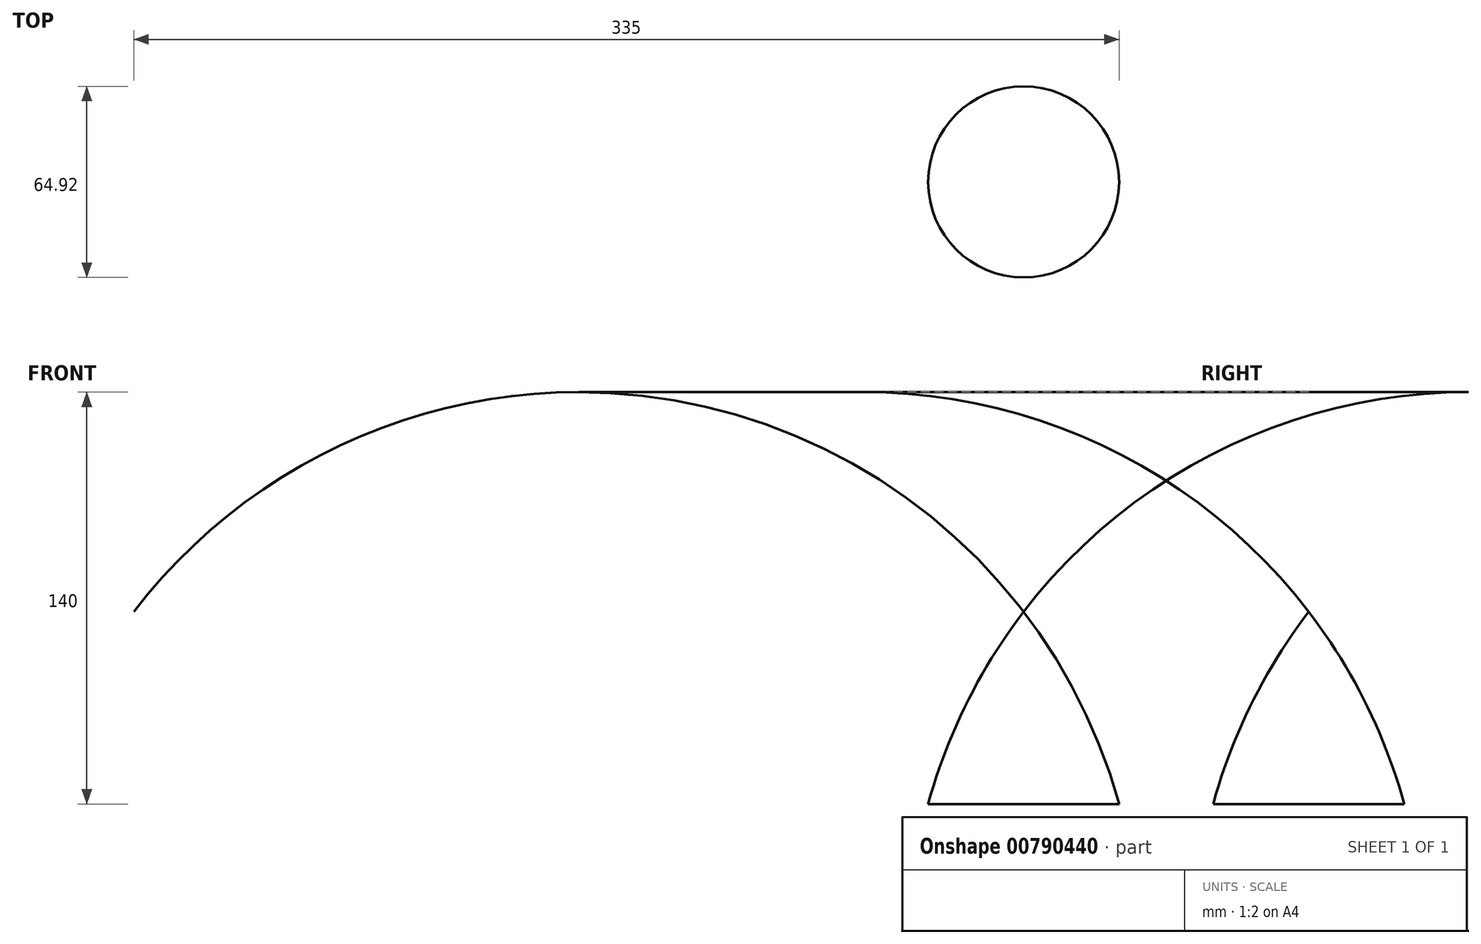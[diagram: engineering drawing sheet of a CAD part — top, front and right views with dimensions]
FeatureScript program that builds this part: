
annotation { "Feature Type Name" : "Feature", "Feature Type Description" : "" }
export const myFeature = defineFeature(function(context is Context, id is Id, definition is map)
    precondition{}
    {
        {
            var Q0;
            Q0=qCreatedBy(makeId("Front.planeOp"),FACE);
            var sketch = newSketch(context, id + "F0", { "sketchPlane" : qUnion([Q0])});
            skLineSegment(sketch, "E0", {"start": v(0, 0) * mm, "end": v(32.46, 0) * mm});
            skLineSegment(sketch, "E1", {"start": v(32.46, 0) * mm, "end": v(32.46, 65.33) * mm});
            skArc(sketch, "E2", {"start": v(32.46, 65.33) * mm, "mid": v(13.07, 34.23) * mm, "end": v(0, 0) * mm});
            skSolve(sketch);
        }
        {
            var Q0;
            Q0 = qSketchRegion(id + "F0", true);
            var Q1;
            Q1=sQuery(id+"F0.wireOp",EDGE,"E1");
            revolve(context, id + "F1", {"surfaceOperationType" : NewSurfaceOperationType.NEW, "entities" : qUnion([Q0]), "axis" : qUnion([Q1]), "revolveType" : RevolveType.FULL});
        }
    });
